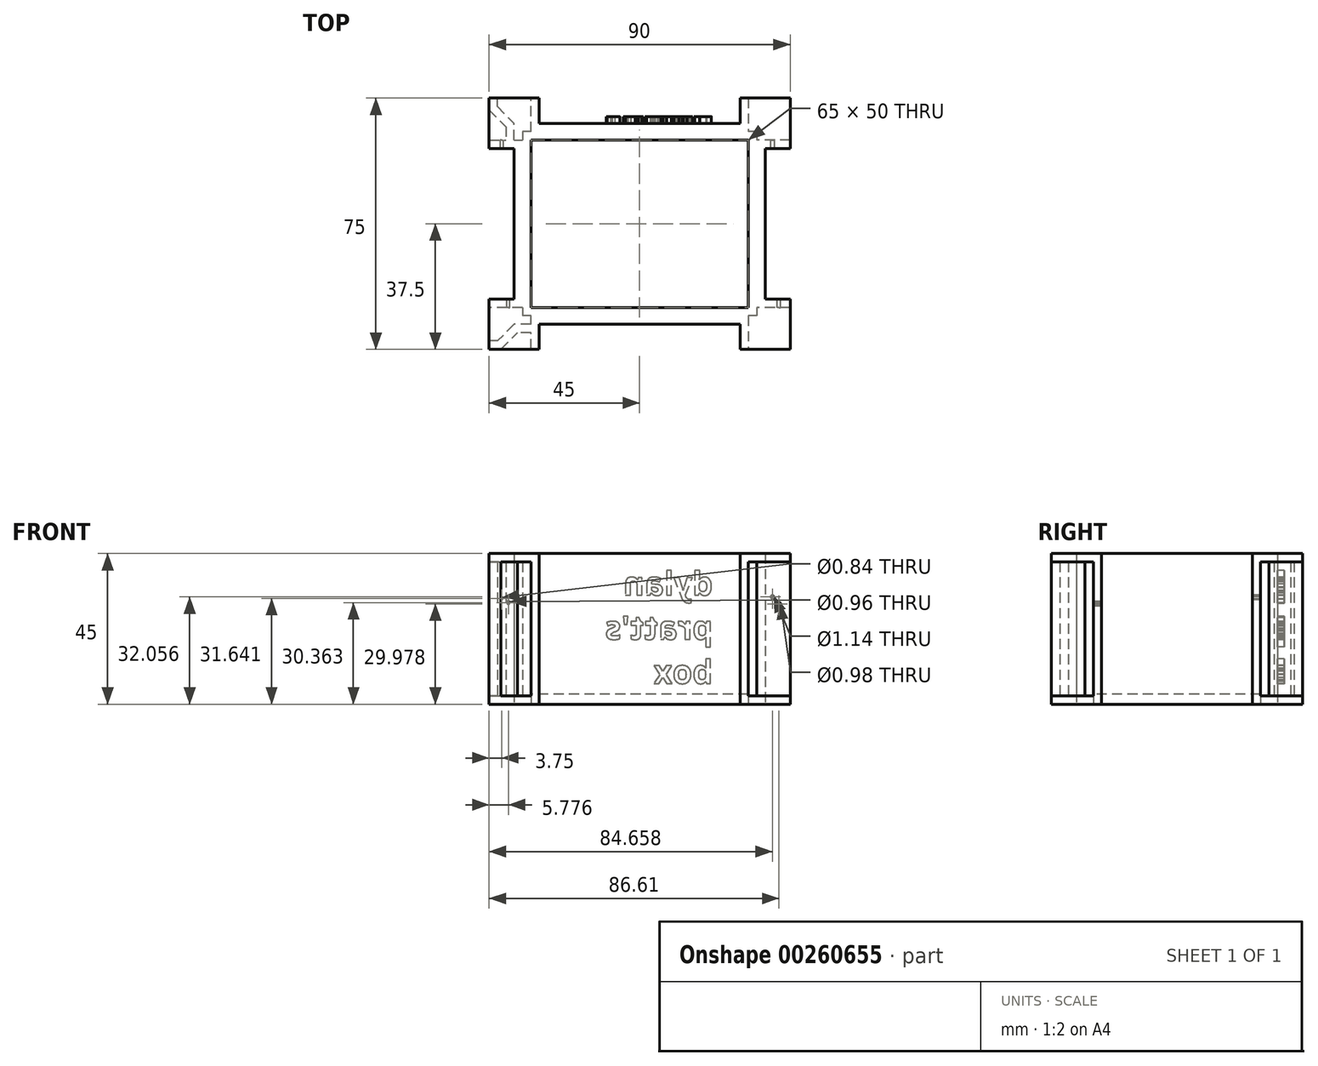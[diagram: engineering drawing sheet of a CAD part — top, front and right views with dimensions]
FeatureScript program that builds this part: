
annotation { "Feature Type Name" : "Feature", "Feature Type Description" : "" }
export const myFeature = defineFeature(function(context is Context, id is Id, definition is map)
    precondition{}
    {
        {
            var Q0;
            Q0=qCreatedBy(makeId("Top.planeOp"),FACE);
            var sketch = newSketch(context, id + "F0", { "sketchPlane" : qUnion([Q0])});
            skLineSegment(sketch, "E0.bottom", {"start": v(37.5, 30) * mm, "end": v(-37.5, 30) * mm});
            skLineSegment(sketch, "E0.top", {"start": v(37.5, -30) * mm, "end": v(-37.5, -30) * mm});
            skLineSegment(sketch, "E0.left", {"start": v(37.5, 30) * mm, "end": v(37.5, -30) * mm});
            skLineSegment(sketch, "E0.right", {"start": v(-37.5, 30) * mm, "end": v(-37.5, -30) * mm});
            skPoint(sketch, "E0.middle", {"position": v(0, 0) * mm});
            skLineSegment(sketch, "E1.bottom", {"start": v(32.5, 25) * mm, "end": v(-32.5, 25) * mm});
            skLineSegment(sketch, "E1.top", {"start": v(32.5, -25) * mm, "end": v(-32.5, -25) * mm});
            skLineSegment(sketch, "E1.left", {"start": v(32.5, 25) * mm, "end": v(32.5, -25) * mm});
            skLineSegment(sketch, "E1.right", {"start": v(-32.5, 25) * mm, "end": v(-32.5, -25) * mm});
            skPoint(sketch, "E2.middle", {"position": v(-37.5, 30) * mm});
            skLineSegment(sketch, "E3.left", {"start": v(42.87, 30) * mm, "end": v(42.87, 30) * mm});
            skLineSegment(sketch, "E3.right", {"start": v(32.13, 30) * mm, "end": v(32.13, 30) * mm});
            skPoint(sketch, "E3.middle", {"position": v(37.5, 30) * mm});
            skLineSegment(sketch, "E4.trimOffspring", {"start": v(-32.5, 25) * mm, "end": v(-32.5, 24.9) * mm});
            skLineSegment(sketch, "E5.bottom", {"start": v(45, 37.5) * mm, "end": v(30, 37.5) * mm});
            skLineSegment(sketch, "E5.top", {"start": v(45, 22.5) * mm, "end": v(37.5, 22.5) * mm});
            skLineSegment(sketch, "E5.left", {"start": v(45, 37.5) * mm, "end": v(45, 22.5) * mm});
            skLineSegment(sketch, "E5.right", {"start": v(30, 37.5) * mm, "end": v(30, 30) * mm});
            skPoint(sketch, "E6.orphan", {"position": v(30, 22.5) * mm});
            skLineSegment(sketch, "E7.bottom", {"start": v(45, -22.5) * mm, "end": v(37.5, -22.5) * mm});
            skLineSegment(sketch, "E7.top", {"start": v(45, -37.5) * mm, "end": v(30, -37.5) * mm});
            skLineSegment(sketch, "E7.left", {"start": v(45, -22.5) * mm, "end": v(45, -37.5) * mm});
            skLineSegment(sketch, "E7.right", {"start": v(30, -30) * mm, "end": v(30, -37.5) * mm});
            skPoint(sketch, "E7.middle", {"position": v(37.5, -30) * mm});
            skLineSegment(sketch, "E8", {"start": v(37.5, 30) * mm, "end": v(45, 37.5) * mm});
            skLineSegment(sketch, "E9", {"start": v(37.5, -30) * mm, "end": v(45, -37.5) * mm});
            skPoint(sketch, "E10.orphan", {"position": v(30, -22.5) * mm});
            skLineSegment(sketch, "E11.bottom", {"start": v(-30, -37.5) * mm, "end": v(-45, -37.5) * mm});
            skLineSegment(sketch, "E11.top", {"start": v(-37.5, -22.5) * mm, "end": v(-45, -22.5) * mm});
            skLineSegment(sketch, "E11.left", {"start": v(-30, -37.5) * mm, "end": v(-30, -30) * mm});
            skLineSegment(sketch, "E11.right", {"start": v(-45, -37.5) * mm, "end": v(-45, -22.5) * mm});
            skPoint(sketch, "E11.middle", {"position": v(-37.5, -30) * mm});
            skPoint(sketch, "E2.bottom.end.orphan", {"position": v(-42.5, 35.1) * mm});
            skPoint(sketch, "E2.left.start.orphan", {"position": v(-32.5, 35.1) * mm});
            skPoint(sketch, "E2.top.end.orphan", {"position": v(-42.5, 24.9) * mm});
            skLineSegment(sketch, "E12.bottom", {"start": v(-45, 22.5) * mm, "end": v(-37.5, 22.5) * mm});
            skLineSegment(sketch, "E12.top", {"start": v(-45, 37.5) * mm, "end": v(-30, 37.5) * mm});
            skLineSegment(sketch, "E12.left", {"start": v(-45, 22.5) * mm, "end": v(-45, 37.5) * mm});
            skLineSegment(sketch, "E12.right", {"start": v(-30, 30) * mm, "end": v(-30, 37.5) * mm});
            skPoint(sketch, "E13.orphan", {"position": v(-30, 22.5) * mm});
            skLineSegment(sketch, "E14", {"start": v(-45, 37.5) * mm, "end": v(-37.5, 30) * mm});
            skLineSegment(sketch, "E15", {"start": v(-45, -37.5) * mm, "end": v(-37.5, -30) * mm});
            skPoint(sketch, "E16.orphan", {"position": v(-30, -22.5) * mm});
            skSolve(sketch);
        }
        {
            var Q0;
            Q0=makeQuery(id+"F0.imprint","IMPRINT",FACE,{"disambiguationData":[TD([[makeQuery(id+"F0.imprint","IMPRINT",EDGE,{"derivedFrom":sQuery(id+"F0.wireOp",EDGE,"E1.bottom")}),-1.0]])]});
            extrude(context, id + "F1", {"entities" : qUnion([Q0]), "depth" : 45 * mm});
        }
        {
            var Q0;
            Q0=makeQuery(id+"F0.imprint","IMPRINT",FACE,{"disambiguationData":[TD([[makeQuery(id+"F0.imprint","IMPRINT",EDGE,{"derivedFrom":sQuery(id+"F0.wireOp",EDGE,"E11.bottom")}),-1.0]])]});
            var Q1;
            {var subQ2=sQuery(id+"F0.wireOp",EDGE,"E12.bottom");Q1=makeQuery(id+"F0.imprint","IMPRINT",FACE,{"disambiguationData":[TD([[makeQuery(id+"F0.imprint","IMPRINT",EDGE,{"derivedFrom":subQ2}),1.0]])]});}
            var Q2;
            Q2=makeQuery(id+"F0.imprint","IMPRINT",FACE,{"disambiguationData":[TD([[makeQuery(id+"F0.imprint","IMPRINT",EDGE,{"derivedFrom":sQuery(id+"F0.wireOp",EDGE,"E5.bottom")}),1.0]])]});
            var Q3;
            {var subQ2=sQuery(id+"F0.wireOp",EDGE,"E7.bottom");Q3=makeQuery(id+"F0.imprint","IMPRINT",FACE,{"disambiguationData":[TD([[makeQuery(id+"F0.imprint","IMPRINT",EDGE,{"derivedFrom":subQ2}),1.0]])]});}
            extrude(context, id + "F2", {"entities" : qUnion([Q0, Q1, Q2, Q3]), "depth" : 45 * mm});
        }
        {
            var Q0;
            Q0=makeQuery(id+"F0.imprint","IMPRINT",FACE,{"disambiguationData":[TD([[makeQuery(id+"F0.imprint","IMPRINT",EDGE,{"derivedFrom":sQuery(id+"F0.wireOp",EDGE,"E1.bottom")}),1.0]])]});
            extrude(context, id + "F3", {"entities" : qUnion([Q0]), "depth" : 3 * mm});
        }
        {
            var Q0;
            Q0=makeQuery(id+"F2.opExtrude","SWEPT_FACE",FACE,{"disambiguationData":[OSD([sQuery(id+"F0.wireOp",EDGE,"E11.bottom")])]});
            var Q1;
            Q1=makeQuery(id+"F5.opExtrude","SWEPT_FACE",FACE,{"disambiguationData":[OSD([sQuery(id+"F0.wireOp",EDGE,"E7.top")])]});
            var Q2;
            Q2=makeQuery(id+"F5.opExtrude","SWEPT_FACE",FACE,{"disambiguationData":[OSD([sQuery(id+"F0.wireOp",EDGE,"E5.left")])]});
            var Q3;
            Q3=makeQuery(id+"F2.opExtrude","SWEPT_FACE",FACE,{"disambiguationData":[OSD([sQuery(id+"F0.wireOp",EDGE,"E12.left")])]});
            shell(context, id + "F4", {"entities" : qUnion([Q0, Q1, Q2, Q3]), "thickness" : 2.5 * mm});
        }
        {
            var Q0;
            Q0=makeQuery(id+"F0.imprint","IMPRINT",FACE,{"disambiguationData":[TD([[makeQuery(id+"F0.imprint","IMPRINT",EDGE,{"derivedFrom":sQuery(id+"F0.wireOp",EDGE,"E12.top")}),-1.0]])]});
            var Q1;
            {var subQ2=sQuery(id+"F0.wireOp",EDGE,"E5.top");Q1=makeQuery(id+"F0.imprint","IMPRINT",FACE,{"disambiguationData":[TD([[makeQuery(id+"F0.imprint","IMPRINT",EDGE,{"derivedFrom":subQ2}),-1.0]])]});}
            var Q2;
            Q2=makeQuery(id+"F0.imprint","IMPRINT",FACE,{"disambiguationData":[TD([[makeQuery(id+"F0.imprint","IMPRINT",EDGE,{"derivedFrom":sQuery(id+"F0.wireOp",EDGE,"E7.top")}),-1.0]])]});
            var Q3;
            {var subQ2=sQuery(id+"F0.wireOp",EDGE,"E11.top");Q3=makeQuery(id+"F0.imprint","IMPRINT",FACE,{"disambiguationData":[TD([[makeQuery(id+"F0.imprint","IMPRINT",EDGE,{"derivedFrom":subQ2}),1.0]])]});}
            extrude(context, id + "F5", {"entities" : qUnion([Q0, Q1, Q2, Q3]), "operationType" : NewBodyOperationType.ADD, "depth" : 45 * mm});
        }
        {
            var Q0;
            Q0=makeQuery(id+"F5.opExtrude","SWEPT_FACE",FACE,{"disambiguationData":[OSD([sQuery(id+"F0.wireOp",EDGE,"E7.top")])]});
            var Q1;
            Q1=makeQuery(id+"F2.opExtrude","SWEPT_FACE",FACE,{"disambiguationData":[OSD([sQuery(id+"F0.wireOp",EDGE,"E7.left")])]});
            var Q2;
            Q2=makeQuery(id+"F5.opExtrude","SWEPT_FACE",FACE,{"disambiguationData":[OSD([sQuery(id+"F0.wireOp",EDGE,"E5.left")])]});
            var Q3;
            Q3=makeQuery(id+"F2.opExtrude","SWEPT_FACE",FACE,{"disambiguationData":[OSD([sQuery(id+"F0.wireOp",EDGE,"E5.bottom")])]});
            var Q4;
            Q4=makeQuery(id+"F5.opExtrude","SWEPT_FACE",FACE,{"disambiguationData":[OSD([sQuery(id+"F0.wireOp",EDGE,"E12.top")])]});
            var Q5;
            Q5=makeQuery(id+"F5.opExtrude","SWEPT_FACE",FACE,{"disambiguationData":[OSD([sQuery(id+"F0.wireOp",EDGE,"E11.right")])]});
            shell(context, id + "F6", {"entities" : qUnion([Q0, Q1, Q2, Q3, Q4, Q5]), "thickness" : 2.5 * mm});
        }
        {
            var Q0;
            Q0=makeQuery(id+"F2.opExtrude","SWEPT_FACE",FACE,{"disambiguationData":[OSD([sQuery(id+"F0.wireOp",EDGE,"E12.bottom")])]});
            var sketch = newSketch(context, id + "F7", { "sketchPlane" : qUnion([Q0])});
            skCircle(sketch, "E17", {"center": v(-41.25, 31.64) * mm, "radius": 0.42 * mm});
            skPoint(sketch, "E17.centerSnap0", {"position": v(-41.25, 45) * mm});
            skSolve(sketch);
        }
        {
            var Q0;
            Q0 = qSketchRegion(id + "F7", true);
            extrude(context, id + "F8", {"entities" : qUnion([Q0]), "operationType" : NewBodyOperationType.REMOVE, "oppositeDirection" : true, "depth" : 3.6 * mm});
        }
        {
            var Q0;
            Q0=makeQuery(id+"F5.opExtrude","SWEPT_FACE",FACE,{"disambiguationData":[OSD([sQuery(id+"F0.wireOp",EDGE,"E11.top")])]});
            var sketch = newSketch(context, id + "F9", { "sketchPlane" : qUnion([Q0])});
            skSolve(sketch);
        }
        {
            var Q0;
            {var subQ0=sQuery(id+"F0.wireOp",EDGE,"E11.top");Q0=makeQuery(id+"F9.imprint","IMPRINT",FACE,{"disambiguationData":[TD([[makeQuery(id+"F9.imprint","IMPRINT",EDGE,{"derivedFrom":makeQuery(id+"F5.opExtrude","CAP_EDGE",EDGE,{"disambiguationData":[OSD([subQ0])],"isStart":true})}),1.0]])]});}
            var sketch = newSketch(context, id + "F10", { "sketchPlane" : qUnion([Q0])});
            skCircle(sketch, "E18", {"center": v(39.22, 30.36) * mm, "radius": 0.48 * mm});
            skSolve(sketch);
        }
        {
            var Q0;
            Q0 = qSketchRegion(id + "F10", true);
            extrude(context, id + "F11", {"entities" : qUnion([Q0]), "operationType" : NewBodyOperationType.REMOVE, "oppositeDirection" : true, "depth" : 3.7 * mm});
        }
        {
            var Q0;
            Q0=makeQuery(id+"F5.opExtrude","SWEPT_FACE",FACE,{"disambiguationData":[OSD([sQuery(id+"F0.wireOp",EDGE,"E5.top")])]});
            var sketch = newSketch(context, id + "F12", { "sketchPlane" : qUnion([Q0])});
            skCircle(sketch, "E19", {"center": v(39.66, 32.06) * mm, "radius": 0.57 * mm});
            skSolve(sketch);
        }
        {
            var Q0;
            Q0 = qSketchRegion(id + "F12", true);
            extrude(context, id + "F13", {"entities" : qUnion([Q0]), "operationType" : NewBodyOperationType.REMOVE, "oppositeDirection" : true, "depth" : 3.5 * mm});
        }
        {
            var Q0;
            Q0=makeQuery(id+"F2.opExtrude","SWEPT_FACE",FACE,{"disambiguationData":[OSD([sQuery(id+"F0.wireOp",EDGE,"E7.bottom")])]});
            var sketch = newSketch(context, id + "F14", { "sketchPlane" : qUnion([Q0])});
            skCircle(sketch, "E20", {"center": v(-41.61, 29.98) * mm, "radius": 0.5 * mm});
            skSolve(sketch);
        }
        {
            var Q0;
            Q0 = qSketchRegion(id + "F14", true);
            extrude(context, id + "F15", {"entities" : qUnion([Q0]), "operationType" : NewBodyOperationType.REMOVE, "oppositeDirection" : true, "depth" : 4.5 * mm});
        }
        {
            var Q0;
            Q0=makeQuery(id+"F1.opExtrude","SWEPT_FACE",FACE,{"disambiguationData":[OSD([sQuery(id+"F0.wireOp",EDGE,"E0.bottom")])]});
            var sketch = newSketch(context, id + "F16", { "sketchPlane" : qUnion([Q0])});
            skText(sketch, "E21", { "text": "dylan\npratt\'s\nbox", "fontName": "OpenSans-Bold.ttf"});
            const initialGuessF16  = {"E21": [-0.02189, 0.03257, 1, 0, 0.00698]};
            skSetInitialGuess(sketch, initialGuessF16);
            skSolve(sketch);
        }
        {
            var Q0;
            Q0 = qSketchRegion(id + "F16", true);
            extrude(context, id + "F17", {"entities" : qUnion([Q0]), "operationType" : NewBodyOperationType.ADD, "depth" : 2 * mm});
        }
    });
